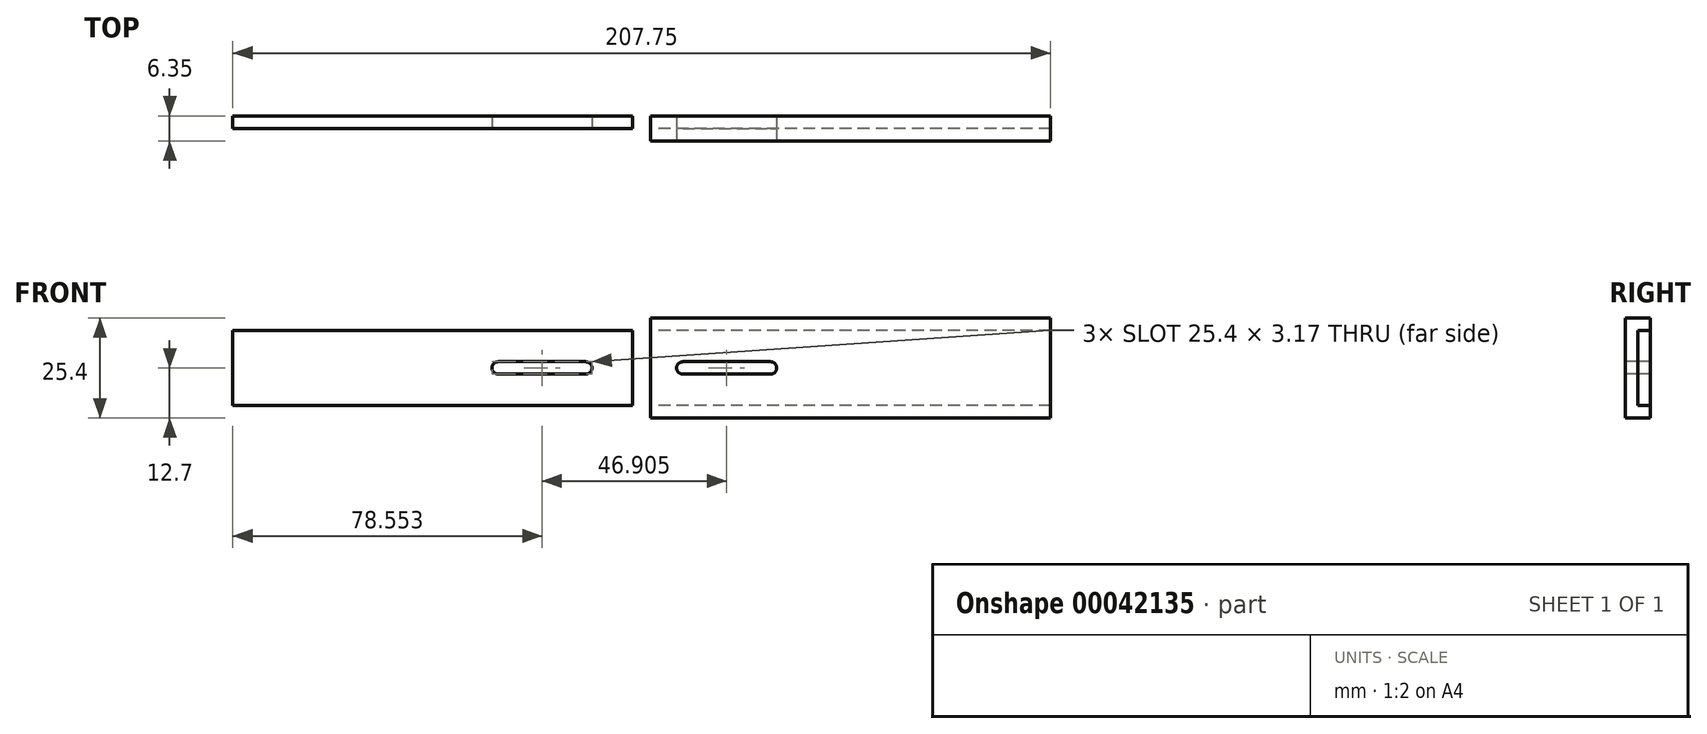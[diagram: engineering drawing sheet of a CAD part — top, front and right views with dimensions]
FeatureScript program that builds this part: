
annotation { "Feature Type Name" : "Feature", "Feature Type Description" : "" }
export const myFeature = defineFeature(function(context is Context, id is Id, definition is map)
    precondition{}
    {
        {
            var Q0;
            Q0=qCreatedBy(makeId("Front.planeOp"),FACE);
            var sketch = newSketch(context, id + "F0", { "sketchPlane" : qUnion([Q0])});
            skLineSegment(sketch, "E0.rect.bottom", {"start": v(0, -9.53) * mm, "end": v(-101.6, -9.53) * mm});
            skLineSegment(sketch, "E0.rect.top", {"start": v(0, 9.52) * mm, "end": v(-101.6, 9.52) * mm});
            skLineSegment(sketch, "E0.rect.left", {"start": v(0, -9.53) * mm, "end": v(0, 9.52) * mm});
            skLineSegment(sketch, "E0.rect.right", {"start": v(-101.6, -9.53) * mm, "end": v(-101.6, 9.52) * mm});
            skPoint(sketch, "E0.rect.middle", {"position": v(-50.8, 0) * mm});
            skSolve(sketch);
        }
        {
            var Q0;
            Q0=makeQuery(id+"F0.imprint","IMPRINT",FACE,{"disambiguationData":[TD([[makeQuery(id+"F0.imprint","IMPRINT",EDGE,{"derivedFrom":sQuery(id+"F0.wireOp",EDGE,"E0.rect.bottom")}),-1.0]])]});
            extrude(context, id + "F1", {"entities" : qUnion([Q0]), "depth" : 3.17 * mm});
        }
        {
            var Q0;
            Q0=makeQuery(id+"F1.opExtrude","SWEPT_BODY",BODY,{"disambiguationData":[OSD([sQuery(id+"F0.wireOp",EDGE,"E0.rect.bottom"),sQuery(id+"F0.wireOp",EDGE,"E0.rect.top"),sQuery(id+"F0.wireOp",EDGE,"E0.rect.left"),sQuery(id+"F0.wireOp",EDGE,"E0.rect.right")])]});
            transform(context, id + "F2", {"entities" : qUnion([Q0]), "transformType" : TransformType.TRANSLATION_3D, "dx" : 106.15 * mm, "dy" : 0 * mm, "dz" : 0 * mm, "makeCopy" : true});
        }
        {
            var Q0;
            Q0=makeQuery(id+"F2.opPattern","COPY",FACE,{"derivedFrom":makeQuery(id+"F1.opExtrude","SWEPT_FACE",FACE,{"disambiguationData":[OSD([sQuery(id+"F0.wireOp",EDGE,"E0.rect.left")])]}),"instanceName":"1"});
            var sketch = newSketch(context, id + "F3", { "sketchPlane" : qUnion([Q0])});
            skLineSegment(sketch, "E1", {"start": v(0, -9.52) * mm, "end": v(-3.18, -9.52) * mm});
            skLineSegment(sketch, "E2", {"start": v(-3.17, -9.52) * mm, "end": v(-3.18, 9.53) * mm});
            skLineSegment(sketch, "E3", {"start": v(-3.18, 9.53) * mm, "end": v(0, 9.53) * mm});
            skLineSegment(sketch, "E4", {"start": v(0, 9.53) * mm, "end": v(0, 12.7) * mm});
            skLineSegment(sketch, "E5", {"start": v(0, 12.7) * mm, "end": v(-6.35, 12.7) * mm});
            skLineSegment(sketch, "E6", {"start": v(-6.35, 12.7) * mm, "end": v(-6.35, -12.7) * mm});
            skLineSegment(sketch, "E7", {"start": v(-6.35, -12.7) * mm, "end": v(0, -12.7) * mm});
            skLineSegment(sketch, "E8", {"start": v(0, -12.7) * mm, "end": v(0, -9.52) * mm});
            skSolve(sketch);
        }
        {
            var Q0;
            Q0 = qSketchRegion(id + "F3", true);
            var Q1;
            Q1=makeQuery(id+"F2.opPattern","COPY",FACE,{"derivedFrom":makeQuery(id+"F1.opExtrude","SWEPT_FACE",FACE,{"disambiguationData":[OSD([sQuery(id+"F0.wireOp",EDGE,"E0.rect.right")])]}),"instanceName":"1"});
            extrude(context, id + "F4", {"entities" : qUnion([Q0]), "endBound" : BoundingType.UP_TO_SURFACE, "oppositeDirection" : true, "endBoundEntityFace" : qUnion([Q1]), "depth" : 25.4 * mm});
        }
        {
            var Q0;
            Q0=makeQuery(id+"F1.opExtrude","CAP_FACE",FACE,{"disambiguationData":[OSD([sQuery(id+"F0.wireOp",EDGE,"E0.rect.bottom"),sQuery(id+"F0.wireOp",EDGE,"E0.rect.top"),sQuery(id+"F0.wireOp",EDGE,"E0.rect.left"),sQuery(id+"F0.wireOp",EDGE,"E0.rect.right")])],"isStart":false});
            var sketch = newSketch(context, id + "F5", { "sketchPlane" : qUnion([Q0])});
            skLineSegment(sketch, "E9.bottom", {"start": v(-34.16, 1.59) * mm, "end": v(-11.93, 1.59) * mm});
            skLineSegment(sketch, "E9.top", {"start": v(-34.16, -1.59) * mm, "end": v(-11.93, -1.59) * mm});
            skLineSegment(sketch, "E9.left", {"start": v(-34.16, 1.59) * mm, "end": v(-34.16, -1.59) * mm});
            skLineSegment(sketch, "E9.right", {"start": v(-11.93, 1.59) * mm, "end": v(-11.93, -1.59) * mm});
            skArc(sketch, "E10", {"start": v(-34.16, 1.59) * mm, "mid": v(-35.75, 0) * mm, "end": v(-34.16, -1.59) * mm});
            skArc(sketch, "E11", {"start": v(-11.93, -1.59) * mm, "mid": v(-10.35, 0) * mm, "end": v(-11.93, 1.59) * mm});
            skSolve(sketch);
        }
        {
            var Q0;
            Q0=makeQuery(id+"F5.imprint","IMPRINT",FACE,{"disambiguationData":[TD([[makeQuery(id+"F5.imprint","IMPRINT",EDGE,{"derivedFrom":sQuery(id+"F5.wireOp",EDGE,"E9.bottom")}),-1.0]])]});
            var Q1;
            Q1=makeQuery(id+"F5.imprint","IMPRINT",FACE,{"disambiguationData":[TD([[makeQuery(id+"F5.imprint","IMPRINT",EDGE,{"derivedFrom":sQuery(id+"F5.wireOp",EDGE,"E9.left")}),-1.0]])]});
            var Q2;
            Q2=makeQuery(id+"F5.imprint","IMPRINT",FACE,{"disambiguationData":[TD([[makeQuery(id+"F5.imprint","IMPRINT",EDGE,{"derivedFrom":sQuery(id+"F5.wireOp",EDGE,"E9.right")}),1.0]])]});
            extrude(context, id + "F6", {"entities" : qUnion([Q0, Q1, Q2]), "operationType" : NewBodyOperationType.REMOVE, "endBound" : BoundingType.THROUGH_ALL, "oppositeDirection" : true, "depth" : 25.4 * mm});
        }
        {
            var Q0;
            Q0=makeQuery(id+"F4.opExtrude","SWEPT_FACE",FACE,{"disambiguationData":[OSD([sQuery(id+"F3.wireOp",EDGE,"E6")])]});
            var sketch = newSketch(context, id + "F7", { "sketchPlane" : qUnion([Q0])});
            skLineSegment(sketch, "E12.bottom", {"start": v(12.75, 1.59) * mm, "end": v(34.97, 1.59) * mm});
            skLineSegment(sketch, "E12.top", {"start": v(12.75, -1.59) * mm, "end": v(34.97, -1.59) * mm});
            skLineSegment(sketch, "E12.left", {"start": v(12.75, 1.59) * mm, "end": v(12.75, -1.59) * mm});
            skLineSegment(sketch, "E12.right", {"start": v(34.97, 1.59) * mm, "end": v(34.97, -1.59) * mm});
            skArc(sketch, "E13", {"start": v(12.75, 1.59) * mm, "mid": v(11.16, 0) * mm, "end": v(12.75, -1.59) * mm});
            skArc(sketch, "E14", {"start": v(34.97, -1.59) * mm, "mid": v(36.56, 0) * mm, "end": v(34.97, 1.59) * mm});
            skLineSegment(sketch, "E15.0", {"start": v(4.55, 9.53) * mm, "end": v(106.15, 9.52) * mm});
            skSolve(sketch);
        }
        {
            var Q0;
            Q0 = qSketchRegion(id + "F7", true);
            extrude(context, id + "F8", {"entities" : qUnion([Q0]), "operationType" : NewBodyOperationType.REMOVE, "oppositeDirection" : true, "depth" : 25.4 * mm});
        }
    });
